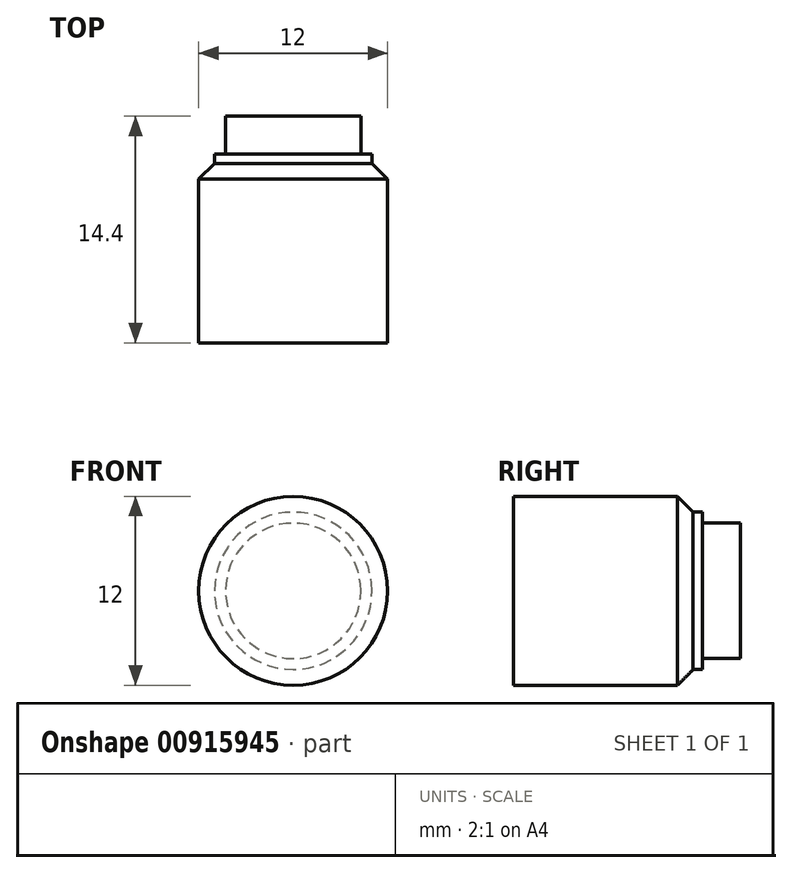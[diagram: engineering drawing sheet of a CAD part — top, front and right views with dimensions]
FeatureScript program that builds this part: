
annotation { "Feature Type Name" : "Feature", "Feature Type Description" : "" }
export const myFeature = defineFeature(function(context is Context, id is Id, definition is map)
    precondition{}
    {
        {
            var Q0;
            Q0=qCreatedBy(makeId("Top.planeOp"),FACE);
            var sketch = newSketch(context, id + "F0", { "sketchPlane" : qUnion([Q0])});
            skLineSegment(sketch, "E0", {"start": v(0, 0) * mm, "end": v(0, 14.4) * mm});
            skLineSegment(sketch, "E1", {"start": v(0, 0) * mm, "end": v(6, 0) * mm});
            skLineSegment(sketch, "E2", {"start": v(6, 0) * mm, "end": v(6, 11.4) * mm});
            skLineSegment(sketch, "E3", {"start": v(6, 11.4) * mm, "end": v(4.3, 11.4) * mm});
            skLineSegment(sketch, "E4", {"start": v(4.3, 11.4) * mm, "end": v(4.3, 14.4) * mm});
            skLineSegment(sketch, "E5", {"start": v(4.3, 14.4) * mm, "end": v(0, 14.4) * mm});
            skLineSegment(sketch, "E6", {"start": v(4.3, 12) * mm, "end": v(5, 12) * mm});
            skLineSegment(sketch, "E7", {"start": v(5, 12) * mm, "end": v(5, 11.4) * mm});
            skSolve(sketch);
        }
        {
            var Q0;
            {var subQ4=sQuery(id+"F0.wireOp",EDGE,"E6");Q0=makeQuery(id+"F0.imprint","IMPRINT",FACE,{"disambiguationData":[TD([[makeQuery(id+"F0.imprint","IMPRINT",EDGE,{"derivedFrom":subQ4}),-1.0]])]});}
            var Q1;
            Q1=makeQuery(id+"F0.imprint","IMPRINT",FACE,{"disambiguationData":[TD([[makeQuery(id+"F0.imprint","IMPRINT",EDGE,{"derivedFrom":sQuery(id+"F0.wireOp",EDGE,"E0")}),-1.0]])]});
            var Q2;
            Q2=sQuery(id+"F0.wireOp",EDGE,"E0");
            revolve(context, id + "F1", {"surfaceOperationType" : NewSurfaceOperationType.NEW, "entities" : qUnion([Q0, Q1]), "axis" : qUnion([Q2]), "revolveType" : RevolveType.FULL});
        }
        {
            var Q0;
            Q0=makeQuery(id+"F1.opRevolve","SWEPT_EDGE",EDGE,{"disambiguationData":[OSD([sQuery(id+"F0.wireOp",EDGE,"E2"),sQuery(id+"F0.wireOp",EDGE,"E3")])]});
            chamfer(context, id + "F2", {"entities" : qUnion([Q0]), "width" : 1 * mm, "tangentPropagation" : true});
        }
    });
